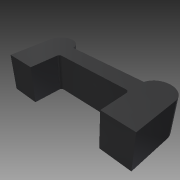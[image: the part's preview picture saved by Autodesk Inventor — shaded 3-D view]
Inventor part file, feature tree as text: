
AUTODESK INVENTOR PART (.ipt)
format: ipt  version: 2015 SP1 (Build 190203100, 203)  size: 1,130,496 bytes
history: native  units: mm
features: extrude x4, sketch x4, projected_geometry x3, other x2, surface_op x1, fillet x1, reference x1
ambient origin geometry x8: Origin, YZ Plane, XZ Plane, XY Plane, X Axis, Y Axis, Z Axis, Center Point
bodies: Solid1 (feature_tree)
feature tree (16):
  extrude  "Extrusion1"  Depth=80.0mm
  surface_op  "Sculpt2"
  extrude  "Extrusion2"  Depth=3.0mm
  extrude  "Extrusion3"  Depth=0.5mm
  extrude  "Extrusion4"  Depth=1.0mm
  fillet  "Fillet1"  Radius=0.5mm
  sketch  "Sketch1"  dims[d0=25.0mm d1=0.0mm d2=80.0mm]
  reference  "Reference1"
  sketch  "Sketch2"  dims[d3=35.0mm d4=3.0mm]
  projected_geometry  "Projected Loop1"
  sketch  "Sketch3"  dims[d5=2.5mm d6=0.5mm]
  projected_geometry  "Projected Loop2"
  sketch  "Sketch4"  dims[d7=0.5mm d8=0.3mm d9=0.5mm d10=0.3mm d12=0.5mm d13=0.3mm d14=0.3mm d16=0.3mm d17=2.0mm d18=0.0mm d19=1.8mm d20=23.25mm d21=0.0mm d23=23.25mm d24=0.0mm d25=1.0mm]
  projected_geometry  "Projected Loop3"
  other  "Composite2"
  other  "Srf2"
